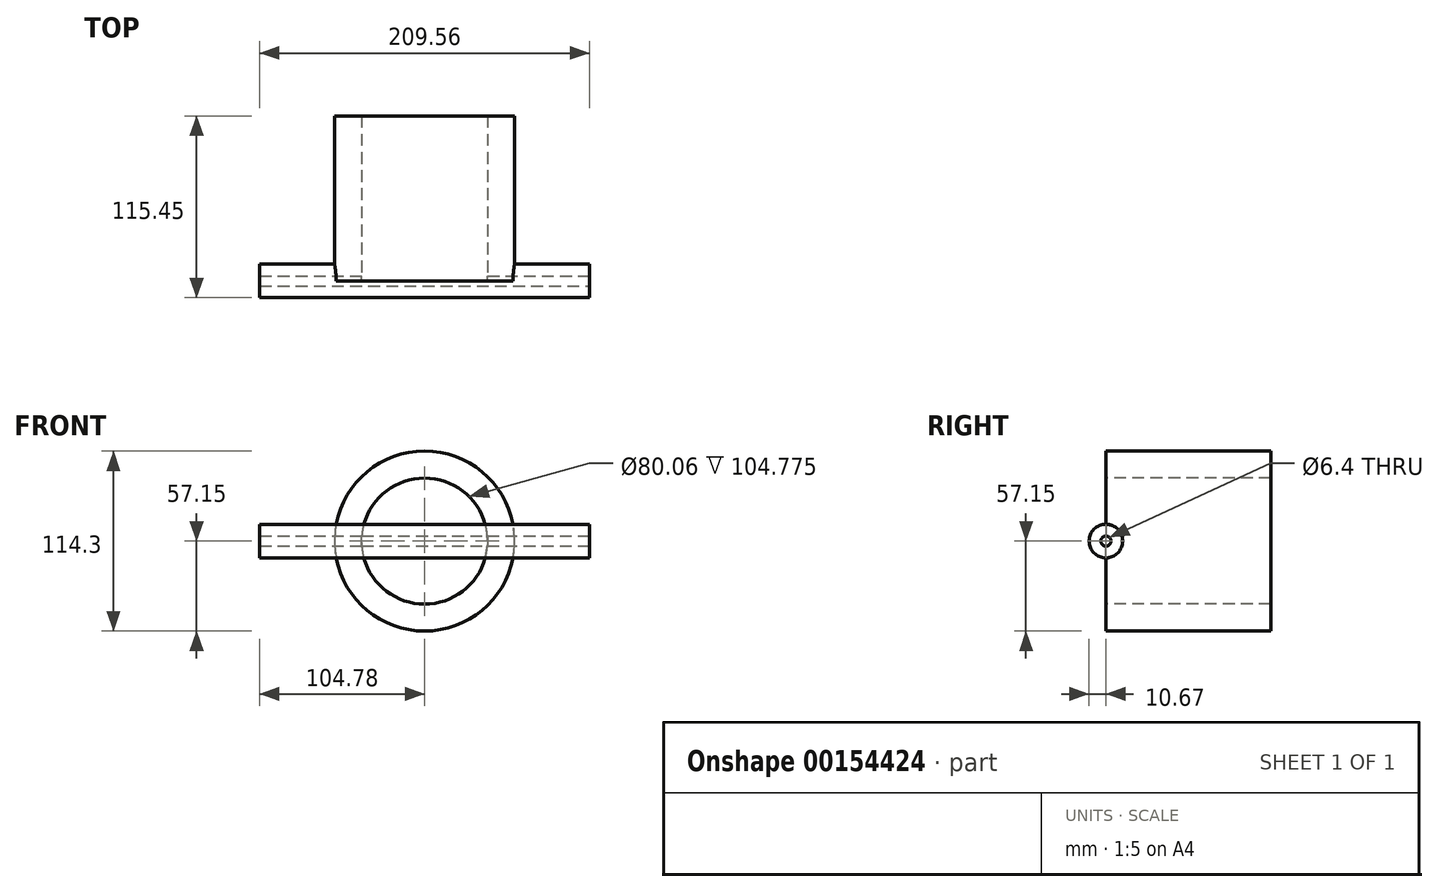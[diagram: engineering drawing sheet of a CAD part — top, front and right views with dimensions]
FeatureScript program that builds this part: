
annotation { "Feature Type Name" : "Feature", "Feature Type Description" : "" }
export const myFeature = defineFeature(function(context is Context, id is Id, definition is map)
    precondition{}
    {
        {
            var Q0;
            Q0=qCreatedBy(makeId("Front.planeOp"),FACE);
            var sketch = newSketch(context, id + "F0", { "sketchPlane" : qUnion([Q0])});
            skCircle(sketch, "E0", {"center": v(0, 0) * mm, "radius": 57.15 * mm});
            skSolve(sketch);
        }
        {
            var Q0;
            Q0=qCreatedBy(makeId("Front.planeOp"),FACE);
            var sketch = newSketch(context, id + "F1", { "sketchPlane" : qUnion([Q0])});
            skCircle(sketch, "E1.0", {"center": v(0, 0) * mm, "radius": 40.03 * mm});
            skSolve(sketch);
        }
        {
            var Q0;
            Q0=qCreatedBy(makeId("Right.planeOp"),FACE);
            var sketch = newSketch(context, id + "F2", { "sketchPlane" : qUnion([Q0])});
            skCircle(sketch, "E2", {"center": v(0, 0) * mm, "radius": 10.67 * mm});
            skSolve(sketch);
        }
        {
            var Q0;
            Q0=makeQuery(id+"F2.imprint","IMPRINT",FACE,{"disambiguationData":[TD([[makeQuery(id+"F2.imprint","IMPRINT",EDGE,{"derivedFrom":sQuery(id+"F2.wireOp",EDGE,"E2")}),1.0]])]});
            extrude(context, id + "F3", {"entities" : qUnion([Q0]), "depth" : 104.77 * mm, "hasSecondDirection" : true, "secondDirectionOppositeDirection" : true, "secondDirectionDepth" : 104.77 * mm});
        }
        {
            var Q0;
            Q0=qSketchRegion(id+"F0",true);
            extrude(context, id + "F4", {"entities" : qUnion([Q0]), "operationType" : NewBodyOperationType.ADD, "oppositeDirection" : true, "depth" : 104.77 * mm});
        }
        {
            var Q0;
            Q0=makeQuery(id+"F3.opExtrude","CAP_FACE",FACE,{"disambiguationData":[OSD([sQuery(id+"F2.wireOp",EDGE,"E2")])],"isStart":false});
            var sketch = newSketch(context, id + "F5", { "sketchPlane" : qUnion([Q0])});
            skCircle(sketch, "E3.0", {"center": v(0, 0) * mm, "radius": 3.2 * mm});
            skSolve(sketch);
        }
        {
            var Q0;
            Q0=makeQuery(id+"F5.imprint","IMPRINT",FACE,{"disambiguationData":[TD([[makeQuery(id+"F5.imprint","IMPRINT",EDGE,{"derivedFrom":sQuery(id+"F5.wireOp",EDGE,"E3.0")}),1.0]])]});
            extrude(context, id + "F6", {"entities" : qUnion([Q0]), "operationType" : NewBodyOperationType.REMOVE, "endBound" : BoundingType.THROUGH_ALL, "oppositeDirection" : true, "depth" : 25.4 * mm});
        }
        {
            var Q0;
            Q0=qSketchRegion(id+"F1",true);
            extrude(context, id + "F7", {"entities" : qUnion([Q0]), "operationType" : NewBodyOperationType.REMOVE, "endBound" : BoundingType.THROUGH_ALL, "oppositeDirection" : true, "depth" : 25.4 * mm});
        }
    });
